# Revit family: Door_Access_Fire-Ceiling_Acudor_FWC-5015
name_source: partatom
category: Generic Models
units: mm (PartAtom-declared; Revit-internal decimal feet)

## family parameters
Can host rebar = No
Cut with Voids When Loaded = No
Host = Face
Part Type = Normal
Room Calculation Point = No
Round Connector Dimension = Use Diameter
Shared = No

## types (8) — shared parameters
Default Elevation = 0' - 0"
Description = Acudor Fire Rated Recessed Flush Ceiling Drywall Access Door - FWC-5015 as Specified
Fire Performance = 90 MIN
Green Building-LEED = http://www.arcat.com
Manufacturer = Acudor Products Inc
Manufacturer Fax = 973-575-5160
Manufacturer Website = http://www.acudor.com
Model = FWC-5015
Product Data = http://www.arcat.com
Revision = R1_2017-03
Sales Information = http://www.acudor.com
Standards Conformance = CAN/ULC S101-14  ;  ASTM E119-16  ;  NFPA 251
URL = http://www.acudor.com
Unit Depth = 0' - 5"
zero-valued in all types: Expected Lifespan (Years), Maintenance Schedule (Months), Warranty Duration (Years)

## per-type parameters (varying)
| type | Clear Opening Height | Clear Opening Width | Door Height | Door Width | Opening Height | Opening Width | Overall Height | Overall Width | Unit Height | Unit Weight | Unit Width |
| 24 x 36 Nom | 2' - 11 27/32" | 1' - 11 7/8" | 3' - 0 1/16" | 2' - 0 1/16" | 3' - 0 9/16" | 2' - 0 9/16" | 3' - 2 1/2" | 2' - 2 1/2" | 3' - 0 3/16" | 44 | 2' - 0 3/16" |
| 24 x 24 Nom | 1' - 11 27/32" | 1' - 11 7/8" | 2' - 0 1/16" | 2' - 0 1/16" | 2' - 0 9/16" | 2' - 0 9/16" | 2' - 2 1/2" | 2' - 2 1/2" | 2' - 0 3/16" | 35 | 2' - 0 3/16" |
| 22 x 36 Nom | 2' - 11 27/32" | 1' - 9 7/8" | 3' - 0 1/16" | 1' - 10 1/16" | 3' - 0 9/16" | 1' - 10 9/16" | 3' - 2 1/2" | 2' - 0 1/2" | 3' - 0 3/16" | 41 | 1' - 10 3/16" |
| 22 x 30 Nom | 2' - 5 27/32" | 1' - 9 7/8" | 2' - 6 1/16" | 1' - 10 1/16" | 2' - 6 9/16" | 1' - 10 9/16" | 2' - 8 1/2" | 2' - 0 1/2" | 2' - 6 3/16" | 38 | 1' - 10 3/16" |
| 18 x 18 Nom | 1' - 5 27/32" | 1' - 6 7/8" | 1' - 6 1/16" | 1' - 6 1/16" | 1' - 6 9/16" | 1' - 6 9/16" | 1' - 8 1/2" | 1' - 8 1/2" | 1' - 6 3/16" | 21 | 1' - 6 3/16" |
| 16 x 16 Nom | 1' - 3 27/32" | 1' - 4 7/8" | 1' - 4 1/16" | 1' - 4 1/16" | 1' - 4 9/16" | 1' - 4 9/16" | 1' - 6 1/2" | 1' - 6 1/2" | 1' - 4 3/16" | 16 | 1' - 4 3/16" |
| 14 x 14 Nom | 1' - 1 27/32" | 1' - 2 7/8" | 1' - 2 1/16" | 1' - 2 1/16" | 1' - 2 9/16" | 1' - 2 9/16" | 1' - 4 1/2" | 1' - 4 1/2" | 1' - 2 3/16" | 14 | 1' - 2 3/16" |
| 12 x 12 Nom | 0' - 11 27/32" | 0' - 11 7/8" | 1' - 0 1/16" | 1' - 0 1/16" | 1' - 0 9/16" | 1' - 0 9/16" | 1' - 2 1/2" | 1' - 2 1/2" | 1' - 0 3/16" | 11 | 1' - 0 3/16" |

## geometry (parser evidence)
native form markers: Sweep x3
no freeform markers — native parametric forms only
